# Revit family: RRVCSAD
name_source: partatom
category: Generic Models
revit_build: Autodesk Revit 2018 (Build: 20190510_1515(x64)
units: mm (PartAtom-declared; Revit-internal decimal feet)

## family parameters
Always vertical = No
Can host rebar = No
Cut with Voids When Loaded = No
Part Type = Normal
Room Calculation Point = No
Round Connector Dimension = Use Diameter
Shared = Yes
Work Plane-Based = Yes

## types (2) — shared parameters
Default Elevation = 48 "
Inner Radius = 2.5 "
Outer Radius = 2.75 "
Rack Material = <By Category>
Width = 5 "

## per-type parameters (varying)
| type | Description | Length | Rack Length | Slot Length |
| RRVCSAD1050 | Rocket Rack Vertical Compact Support Assembly 304 1/2-13 Double 10.5 Inch Slot | 11.75 " | 14.5 " | 10.5 " |
| RRVCSAD0650 | Rocket Rack Vertical Compact Support Assembly 304 1/2-13 Double 6.5 Inch Slot | 7.75 " | 10.5 " | 6.5 " |

note: column(s) folded — value = type name in every type: Catalog Number

## geometry (parser evidence)
native form markers: Sweep x8
no freeform markers — native parametric forms only
